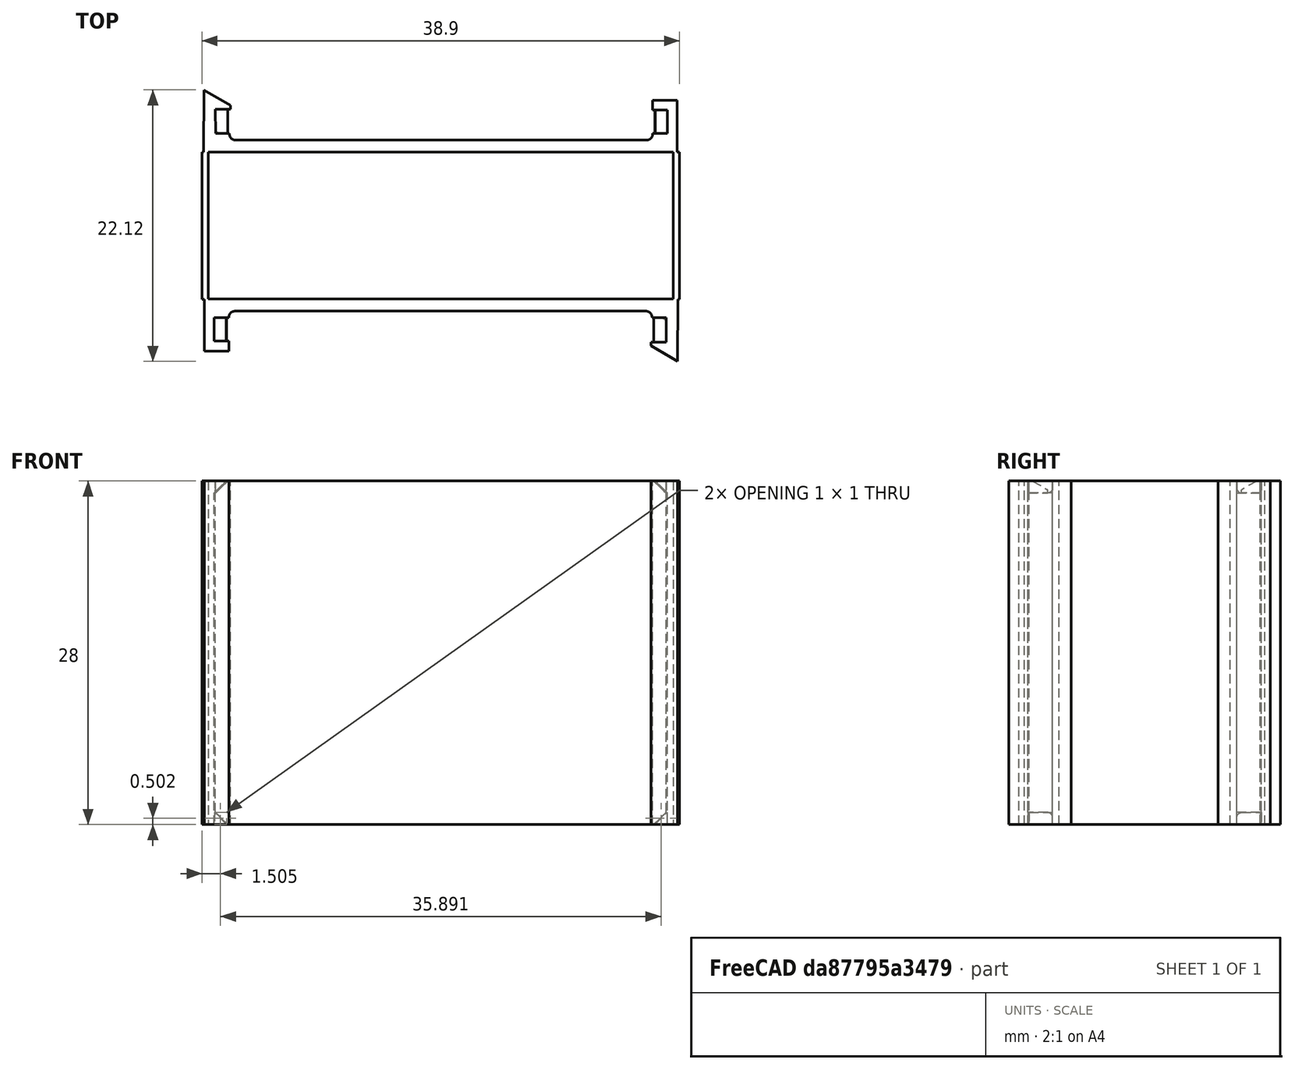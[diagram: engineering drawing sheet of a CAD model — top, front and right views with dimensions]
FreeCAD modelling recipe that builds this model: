
FCSTD DOCUMENT  (FreeCAD 0.18.4R)
Label: GPSBoardClip3
License: All rights reserved
LicenseURL: http://en.wikipedia.org/wiki/All_rights_reserved
objects: Sketcher::SketchObject×10, PartDesign::Pad×10, Part::Fillet×6, Part::MultiFuse×3, Part::Box×2, Mesh::Feature×1
note: 41 computed .brp shape members not serialized (recipe doc carries the construction recipe); baked Part::Feature solids carry a one-line shape summary decoded from their .brp

FEATURE [Sketcher::SketchObject] Sketch
  MapMode = 5
  sketch-geometry (16):
    g0: LineSegment StartX=-17.4674 StartY=-7.02844 StartZ=0 EndX=17.02 EndY=-7.02844 EndZ=0
    g1: LineSegment StartX=18.9972 StartY=-8.01786 StartZ=0 EndX=-19.5785 EndY=-8.01786 EndZ=0
    g2: LineSegment StartX=-17.4674 StartY=-6.49011 StartZ=0 EndX=-17.4674 EndY=-7.02844 EndZ=0
    g3: LineSegment StartX=19.0009 StartY=-3.77022 StartZ=0 EndX=18.9972 EndY=-8.01786 EndZ=0
    g4: LineSegment StartX=16.9998 StartY=-3.76858 StartZ=0 EndX=17.0033 EndY=-4.58507 EndZ=0
    g5: LineSegment StartX=16.9998 StartY=-3.76858 StartZ=0 EndX=19.0009 EndY=-3.77022 EndZ=0
    g6: LineSegment StartX=17.0033 StartY=-4.58507 StartZ=0 EndX=18.2249 EndY=-4.58482 EndZ=0
    g7: LineSegment StartX=18.2249 StartY=-4.58482 StartZ=0 EndX=18.227 EndY=-6.4933 EndZ=0
    g8: LineSegment StartX=18.227 StartY=-6.4933 StartZ=0 EndX=17.0164 EndY=-6.4933 EndZ=0
    g9: LineSegment StartX=17.0164 StartY=-6.4933 StartZ=0 EndX=17.02 EndY=-7.02844 EndZ=0
    g10: LineSegment StartX=-17.4674 StartY=-6.49011 StartZ=0 EndX=-18.6023 EndY=-6.49011 EndZ=0
    g11: LineSegment StartX=-18.6023 StartY=-6.49011 StartZ=0 EndX=-18.6091 EndY=-4.50157 EndZ=0
    g12: LineSegment StartX=-18.6091 StartY=-4.50157 StartZ=0 EndX=-17.3894 EndY=-4.5012 EndZ=0
    g13: LineSegment StartX=-17.3894 StartY=-4.5012 StartZ=0 EndX=-17.3861 EndY=-4.20382 EndZ=0
    g14: LineSegment StartX=-17.3861 StartY=-4.20382 StartZ=0 EndX=-19.5501 EndY=-2.94122 EndZ=0
    g15: LineSegment StartX=-19.5501 StartY=-2.94122 StartZ=0 EndX=-19.5785 EndY=-8.01786 EndZ=0
  constraints (19):
    c: Horizontal(g0)
    c: Horizontal(g1)
    c: Vertical(g2)
    c: Coincident(g1,g3)
    c: Coincident(g5,g4)
    c: Coincident(g4,g6)
    c: Coincident(g6,g7)
    c: Coincident(g7,g8)
    c: Coincident(g0,g9)
    c: Coincident(g9,g8)
    c: Coincident(g5,g3)
    c: Coincident(g10,g2)
    c: Coincident(g10,g11)
    c: Coincident(g11,g12)
    c: Coincident(g12,g13)
    c: Coincident(g13,g14)
    c: Coincident(g2,g0)
    c: Coincident(g15,g14)
    c: Coincident(g15,g1)
FEATURE [PartDesign::Pad] Pad
  Length = 28
  Length2 = 100
  Profile = -> Sketch
  Type = 0
FEATURE [Sketcher::SketchObject] Sketch004
  MapMode = 5
  Placement = pos=(-11.64,-4.5,6.03) rot=(1,0,0;1.5708rad)
  sketch-geometry (3):
    g0: LineSegment StartX=-7.00166 StartY=-5.01077 StartZ=0 EndX=-6.98953 EndY=-6.02972 EndZ=0
    g1: LineSegment StartX=-6.98953 StartY=-6.02972 StartZ=0 EndX=-5.96627 EndY=-6.02972 EndZ=0
    g2: LineSegment StartX=-7.00166 StartY=-5.01077 StartZ=0 EndX=-5.96627 EndY=-6.02972 EndZ=0
  constraints (3):
    c: Coincident(g0,g1)
    c: Coincident(g2,g0)
    c: Coincident(g2,g1)
FEATURE [PartDesign::Pad] Pad004  label="stopper002"
  Length = 2.2
  Length2 = 100
  Placement = pos=(-11.64,-4.5,6.03) rot=(1,0,0;1.5708rad)
  Profile = -> Sketch004
  Type = 0
FEATURE [Sketcher::SketchObject] Sketch006
  MapMode = 5
  Placement = pos=(18.2,-4.5,0.03) rot=(1,0,0;1.5708rad)
  sketch-geometry (3):
    g0: LineSegment StartX=-0.005347 StartY=0.971544 StartZ=0 EndX=-0.005347 EndY=-0.027131 EndZ=0
    g1: LineSegment StartX=-0.005347 StartY=-0.027131 StartZ=0 EndX=-1.00402 EndY=-0.027124 EndZ=0
    g2: LineSegment StartX=-1.00402 StartY=-0.027124 StartZ=0 EndX=-0.005347 EndY=0.971544 EndZ=0
  constraints (3):
    c: Coincident(g0,g1)
    c: Coincident(g1,g2)
    c: Coincident(g2,g0)
FEATURE [PartDesign::Pad] Pad006  label="stopper003"
  Length = 2.2
  Length2 = 100
  Placement = pos=(18.2,-4.5,0.03) rot=(1,0,0;1.5708rad)
  Profile = -> Sketch006
  Type = 0
FEATURE [Sketcher::SketchObject] Sketch007
  MapMode = 5
  Placement = pos=(18.25,-4.5,27.02) rot=(1,0,0;1.5708rad)
  sketch-geometry (3):
    g0: LineSegment StartX=-0.005347 StartY=0.971544 StartZ=0 EndX=-0.005347 EndY=-0.027131 EndZ=0
    g1: LineSegment StartX=-0.005347 StartY=-0.027131 StartZ=0 EndX=-1.00779 EndY=0.969763 EndZ=0
    g2: LineSegment StartX=-1.00779 StartY=0.969763 StartZ=0 EndX=-0.005347 EndY=0.971544 EndZ=0
  constraints (3):
    c: Coincident(g0,g1)
    c: Coincident(g1,g2)
    c: Coincident(g2,g0)
FEATURE [PartDesign::Pad] Pad007  label="stopper004"
  Length = 2.2
  Length2 = 100
  Placement = pos=(18.25,-4.5,27.02) rot=(1,0,0;1.5708rad)
  Profile = -> Sketch007
  Type = 0
FEATURE [Sketcher::SketchObject] Sketch008
  MapMode = 5
  Placement = pos=(-17.6,-4.5,27.02) rot=(1,0,0;1.5708rad)
  sketch-geometry (3):
    g0: LineSegment StartX=-0.005347 StartY=0.971544 StartZ=0 EndX=-1.00207 EndY=-0.002707 EndZ=0
    g1: LineSegment StartX=-1.00207 StartY=-0.002707 StartZ=0 EndX=-1.00779 EndY=0.969763 EndZ=0
    g2: LineSegment StartX=-1.00779 StartY=0.969763 StartZ=0 EndX=-0.005347 EndY=0.971544 EndZ=0
  constraints (3):
    c: Coincident(g0,g1)
    c: Coincident(g1,g2)
    c: Coincident(g2,g0)
FEATURE [PartDesign::Pad] Pad008  label="stopper001"
  Length = 2.2
  Length2 = 100
  Placement = pos=(-17.6,-4.5,27.02) rot=(1,0,0;1.5708rad)
  Profile = -> Sketch008
  Type = 0
FEATURE [Part::MultiFuse] Fusion
  Shapes = -> [Pad,Pad004,Pad006,Pad007,Pad008]
FEATURE [Part::Fillet] Fillet
  Base = -> Fusion
  Edges = 1 edges r=0.5: [Edge15]
FEATURE [Part::Fillet] Fillet001
  Base = -> Fillet
  Edges = 1 edges r=0.5: [Edge3]
FEATURE [Part::Fillet] Fillet002
  Base = -> Fillet001
  Edges = 1 edges r=0.4: [Edge46]
FEATURE [Sketcher::SketchObject] Sketch009
  MapMode = 5
  sketch-geometry (16):
    g0: LineSegment StartX=-17.4674 StartY=-7.02844 StartZ=0 EndX=17.02 EndY=-7.02844 EndZ=0
    g1: LineSegment StartX=18.9972 StartY=-8.01786 StartZ=0 EndX=-19.5785 EndY=-8.01786 EndZ=0
    g2: LineSegment StartX=-17.4674 StartY=-6.49011 StartZ=0 EndX=-17.4674 EndY=-7.02844 EndZ=0
    g3: LineSegment StartX=19.0009 StartY=-3.77022 StartZ=0 EndX=18.9972 EndY=-8.01786 EndZ=0
    g4: LineSegment StartX=16.9998 StartY=-3.76858 StartZ=0 EndX=17.0033 EndY=-4.58507 EndZ=0
    g5: LineSegment StartX=16.9998 StartY=-3.76858 StartZ=0 EndX=19.0009 EndY=-3.77022 EndZ=0
    g6: LineSegment StartX=17.0033 StartY=-4.58507 StartZ=0 EndX=18.2249 EndY=-4.58482 EndZ=0
    g7: LineSegment StartX=18.2249 StartY=-4.58482 StartZ=0 EndX=18.227 EndY=-6.4933 EndZ=0
    g8: LineSegment StartX=18.227 StartY=-6.4933 StartZ=0 EndX=17.0164 EndY=-6.4933 EndZ=0
    g9: LineSegment StartX=17.0164 StartY=-6.4933 StartZ=0 EndX=17.02 EndY=-7.02844 EndZ=0
    g10: LineSegment StartX=-17.4674 StartY=-6.49011 StartZ=0 EndX=-18.6023 EndY=-6.49011 EndZ=0
    g11: LineSegment StartX=-18.6023 StartY=-6.49011 StartZ=0 EndX=-18.6091 EndY=-4.50157 EndZ=0
    g12: LineSegment StartX=-18.6091 StartY=-4.50157 StartZ=0 EndX=-17.3894 EndY=-4.5012 EndZ=0
    g13: LineSegment StartX=-17.3894 StartY=-4.5012 StartZ=0 EndX=-17.3861 EndY=-4.20382 EndZ=0
    g14: LineSegment StartX=-17.3861 StartY=-4.20382 StartZ=0 EndX=-19.5501 EndY=-2.94122 EndZ=0
    g15: LineSegment StartX=-19.5501 StartY=-2.94122 StartZ=0 EndX=-19.5785 EndY=-8.01786 EndZ=0
  constraints (19):
    c: Horizontal(g0)
    c: Horizontal(g1)
    c: Vertical(g2)
    c: Coincident(g1,g3)
    c: Coincident(g5,g4)
    c: Coincident(g4,g6)
    c: Coincident(g6,g7)
    c: Coincident(g7,g8)
    c: Coincident(g0,g9)
    c: Coincident(g9,g8)
    c: Coincident(g5,g3)
    c: Coincident(g10,g2)
    c: Coincident(g10,g11)
    c: Coincident(g11,g12)
    c: Coincident(g12,g13)
    c: Coincident(g13,g14)
    c: Coincident(g2,g0)
    c: Coincident(g15,g14)
    c: Coincident(g15,g1)
FEATURE [PartDesign::Pad] Pad009
  Length = 28
  Length2 = 100
  Profile = -> Sketch009
  Type = 0
FEATURE [Sketcher::SketchObject] Sketch010
  MapMode = 5
  Placement = pos=(-11.64,-4.5,6.03) rot=(1,0,0;1.5708rad)
  sketch-geometry (3):
    g0: LineSegment StartX=-7.00166 StartY=-5.01077 StartZ=0 EndX=-6.98953 EndY=-6.02972 EndZ=0
    g1: LineSegment StartX=-6.98953 StartY=-6.02972 StartZ=0 EndX=-5.96627 EndY=-6.02972 EndZ=0
    g2: LineSegment StartX=-7.00166 StartY=-5.01077 StartZ=0 EndX=-5.96627 EndY=-6.02972 EndZ=0
  constraints (3):
    c: Coincident(g0,g1)
    c: Coincident(g2,g0)
    c: Coincident(g2,g1)
FEATURE [PartDesign::Pad] Pad010  label="stopper005"
  Length = 2.2
  Length2 = 100
  Placement = pos=(-11.64,-4.5,6.03) rot=(1,0,0;1.5708rad)
  Profile = -> Sketch010
  Type = 0
FEATURE [Sketcher::SketchObject] Sketch011
  MapMode = 5
  Placement = pos=(18.2,-4.5,0.03) rot=(1,0,0;1.5708rad)
  sketch-geometry (3):
    g0: LineSegment StartX=-0.005347 StartY=0.971544 StartZ=0 EndX=-0.005347 EndY=-0.027131 EndZ=0
    g1: LineSegment StartX=-0.005347 StartY=-0.027131 StartZ=0 EndX=-1.00402 EndY=-0.027124 EndZ=0
    g2: LineSegment StartX=-1.00402 StartY=-0.027124 StartZ=0 EndX=-0.005347 EndY=0.971544 EndZ=0
  constraints (3):
    c: Coincident(g0,g1)
    c: Coincident(g1,g2)
    c: Coincident(g2,g0)
FEATURE [PartDesign::Pad] Pad011  label="stopper006"
  Length = 2.2
  Length2 = 100
  Placement = pos=(18.2,-4.5,0.03) rot=(1,0,0;1.5708rad)
  Profile = -> Sketch011
  Type = 0
FEATURE [Sketcher::SketchObject] Sketch012
  MapMode = 5
  Placement = pos=(18.25,-4.5,27.02) rot=(1,0,0;1.5708rad)
  sketch-geometry (3):
    g0: LineSegment StartX=-0.005347 StartY=0.971544 StartZ=0 EndX=-0.005347 EndY=-0.027131 EndZ=0
    g1: LineSegment StartX=-0.005347 StartY=-0.027131 StartZ=0 EndX=-1.00779 EndY=0.969763 EndZ=0
    g2: LineSegment StartX=-1.00779 StartY=0.969763 StartZ=0 EndX=-0.005347 EndY=0.971544 EndZ=0
  constraints (3):
    c: Coincident(g0,g1)
    c: Coincident(g1,g2)
    c: Coincident(g2,g0)
FEATURE [PartDesign::Pad] Pad012  label="stopper007"
  Length = 2.2
  Length2 = 100
  Placement = pos=(18.25,-4.5,27.02) rot=(1,0,0;1.5708rad)
  Profile = -> Sketch012
  Type = 0
FEATURE [Sketcher::SketchObject] Sketch013
  MapMode = 5
  Placement = pos=(-17.6,-4.5,27.02) rot=(1,0,0;1.5708rad)
  sketch-geometry (3):
    g0: LineSegment StartX=-0.005347 StartY=0.971544 StartZ=0 EndX=-1.00207 EndY=-0.002707 EndZ=0
    g1: LineSegment StartX=-1.00207 StartY=-0.002707 StartZ=0 EndX=-1.00779 EndY=0.969763 EndZ=0
    g2: LineSegment StartX=-1.00779 StartY=0.969763 StartZ=0 EndX=-0.005347 EndY=0.971544 EndZ=0
  constraints (3):
    c: Coincident(g0,g1)
    c: Coincident(g1,g2)
    c: Coincident(g2,g0)
FEATURE [PartDesign::Pad] Pad013  label="stopper008"
  Length = 2.2
  Length2 = 100
  Placement = pos=(-17.6,-4.5,27.02) rot=(1,0,0;1.5708rad)
  Profile = -> Sketch013
  Type = 0
FEATURE [Part::MultiFuse] Fusion001
  Shapes = -> [Pad009,Pad010,Pad011,Pad012,Pad013]
FEATURE [Part::Fillet] Fillet005
  Base = -> Fusion001
  Edges = 1 edges r=0.5: [Edge15]
FEATURE [Part::Fillet] Fillet004
  Base = -> Fillet005
  Edges = 1 edges r=0.5: [Edge3]
FEATURE [Part::Fillet] Fillet003
  Base = -> Fillet004
  Edges = 1 edges r=0.4: [Edge46]
  Placement = pos=(-0.5,-28,0) rot=(0,0,1;3.14159rad)
FEATURE [Part::Box] Box  label="Würfel002"
  AttacherType = Attacher::AttachEngine3D
  Height = 28
  Length = 0.5
  Placement = pos=(18.7,-20,0) rot=(0,0,1;0rad)
  Width = 12
FEATURE [Part::Box] Box001  label="Würfel001"
  AttacherType = Attacher::AttachEngine3D
  Height = 28
  Length = 0.5
  Placement = pos=(-19.7,-20,0) rot=(0,0,1;0rad)
  Width = 12
FEATURE [Part::MultiFuse] Fusion002
  Shapes = -> [Fillet002,Fillet003,Box,Box001]
FEATURE [Mesh::Feature] Mesh  label="Fusion002 (Meshed)"
